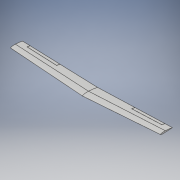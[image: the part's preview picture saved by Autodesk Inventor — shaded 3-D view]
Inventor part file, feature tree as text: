
AUTODESK INVENTOR PART (.ipt)
format: ipt  version: 2019.4 (Build 234330000, 330)  size: 292,352 bytes
history: native  units: mm
features: other x8, sketch x3, plane x2, mirror x2, loft x1, extrude x1
ambient origin geometry x8: Origin, YZ Plane, XZ Plane, XY Plane, X Axis, Y Axis, Z Axis, Center Point
bodies: Solid1 (feature_tree)
feature tree (17):
  sketch  "Sketch1"  dims[d8=0.0mm d9=4.0mm d10=4.0mm]
  plane  "Work Plane1"
  loft  "Loft1"
  mirror  "Mirror1"
  extrude  "Extrusion1"  Depth=4.0mm TaperAngle=0.0deg
  mirror  "Mirror2"
  plane  "Work Plane2"
  other  "2D Equation Curve5"
  other  "2D Equation Curve6"
  other  "2D Equation Curve8"
  other  "2D Equation Curve9"
  sketch  "Sketch2"  dims[d11=10.0mm d14=0.0mm d15=4.0mm]
  other  "2D Equation Curve10"
  other  "2D Equation Curve11"
  other  "2D Equation Curve12"
  other  "2D Equation Curve13"
  sketch  "Sketch4"  dims[d16=4.0mm d17=10.0mm d18=5000.0mm d19=0.0mm d20=4.0mm d21=4.0mm d22=10.0mm d23=0.0mm d24=4.0mm d25=4.0mm d26=10.0mm d27=0.0mm d28=90.0deg d29=0.0mm d30=90.0deg d35=2500.0mm d36=775.0mm d37=4500.0mm d38=795.0mm d40=1000.0mm d41=0.0mm d42=600.0mm d43=600.0mm d49=200.0mm]
